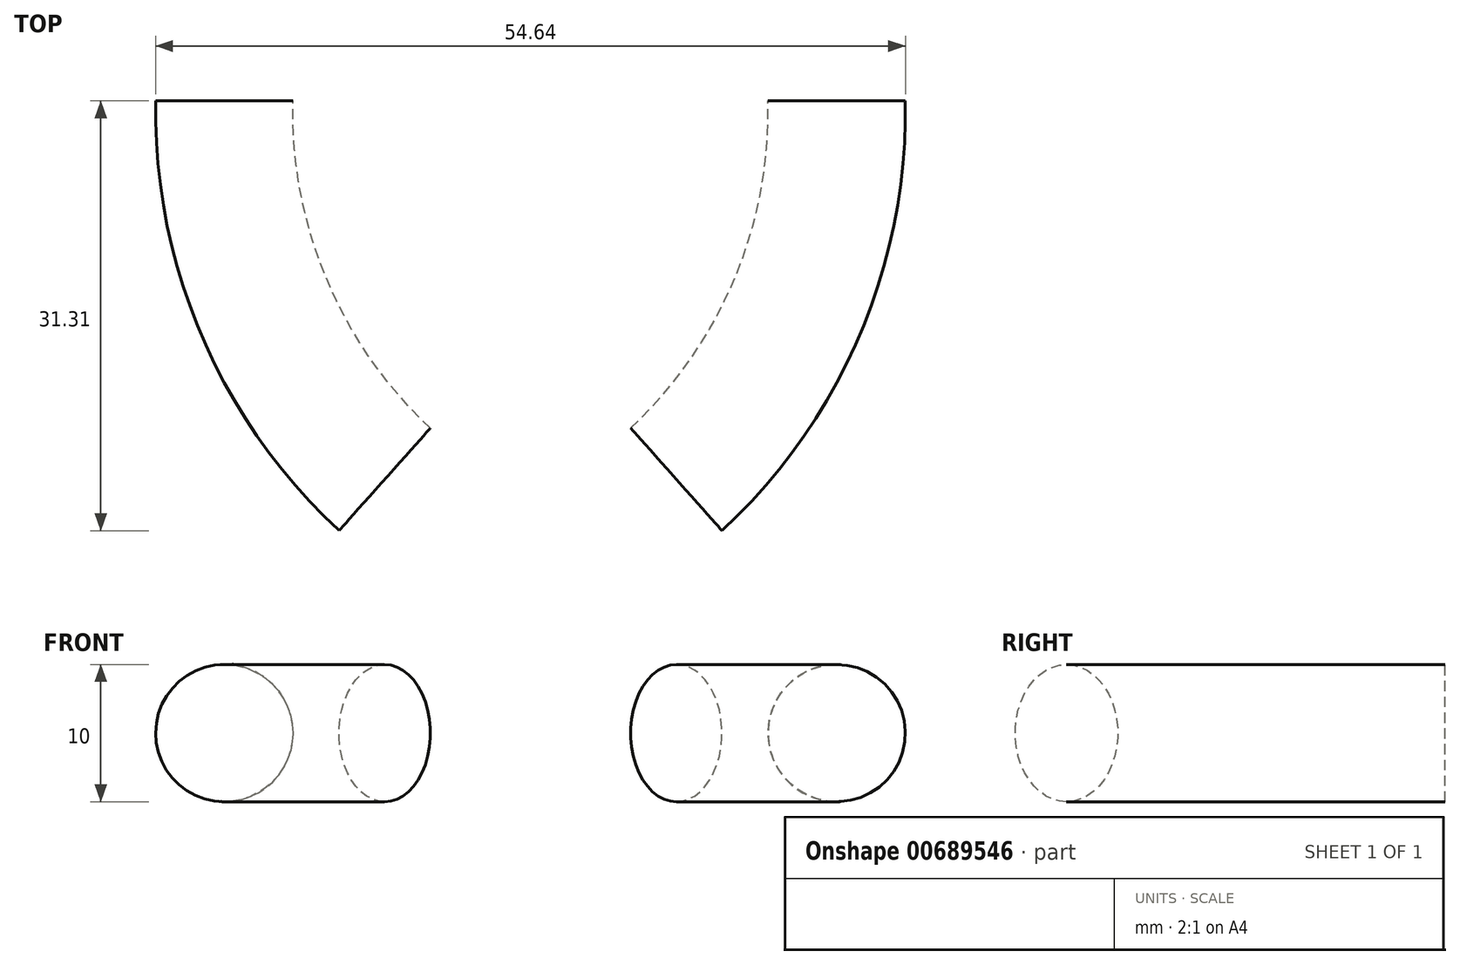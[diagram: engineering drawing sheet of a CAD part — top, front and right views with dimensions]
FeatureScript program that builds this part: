
annotation { "Feature Type Name" : "Feature", "Feature Type Description" : "" }
export const myFeature = defineFeature(function(context is Context, id is Id, definition is map)
    precondition{}
    {
        {
            var Q0;
            Q0=qCreatedBy(makeId("Top.planeOp"),FACE);
            var sketch = newSketch(context, id + "F0", { "sketchPlane" : qUnion([Q0])});
            skArc(sketch, "E0", {"start": v(10.42, -27.34) * mm, "mid": v(19.13, -14.91) * mm, "end": v(22, 0) * mm});
            skArc(sketch, "E1.MirrorCS", {"start": v(-10.42, -27.34) * mm, "mid": v(-19.13, -14.91) * mm, "end": v(-22, 0) * mm});
            skSolve(sketch);
        }
        {
            var Q0;
            Q0=qCreatedBy(makeId("Front.planeOp"),FACE);
            var sketch = newSketch(context, id + "F1", { "sketchPlane" : qUnion([Q0])});
            skCircle(sketch, "E2", {"center": v(22.3, 0) * mm, "radius": 5 * mm});
            skCircle(sketch, "E3.MirrorC", {"center": v(-22.3, 0) * mm, "radius": 5 * mm});
            skSolve(sketch);
        }
        {
            var Q0;
            Q0=makeQuery(id+"F1.imprint","IMPRINT",FACE,{"disambiguationData":[TD([[makeQuery(id+"F1.imprint","IMPRINT",EDGE,{"derivedFrom":sQuery(id+"F1.wireOp",EDGE,"E2")}),1.0]])]});
            var Q1;
            Q1=sQuery(id+"F0.wireOp",EDGE,"E0");
            sweep(context, id + "F2", {"profiles" : qUnion([Q0]), "path" : qUnion([Q1])});
        }
        {
            var Q0;
            Q0=makeQuery(id+"F2.opSweep","SWEPT_BODY",BODY,{"disambiguationData":[OSD([sQuery(id+"F0.wireOp",EDGE,"E0"),sQuery(id+"F1.wireOp",EDGE,"E2")])]});
            var Q1;
            Q1=qCreatedBy(makeId("Right.planeOp"),FACE);
            mirror(context, id + "F3", {"entities" : qUnion([Q0]), "mirrorPlane" : qUnion([Q1])});
        }
    });
